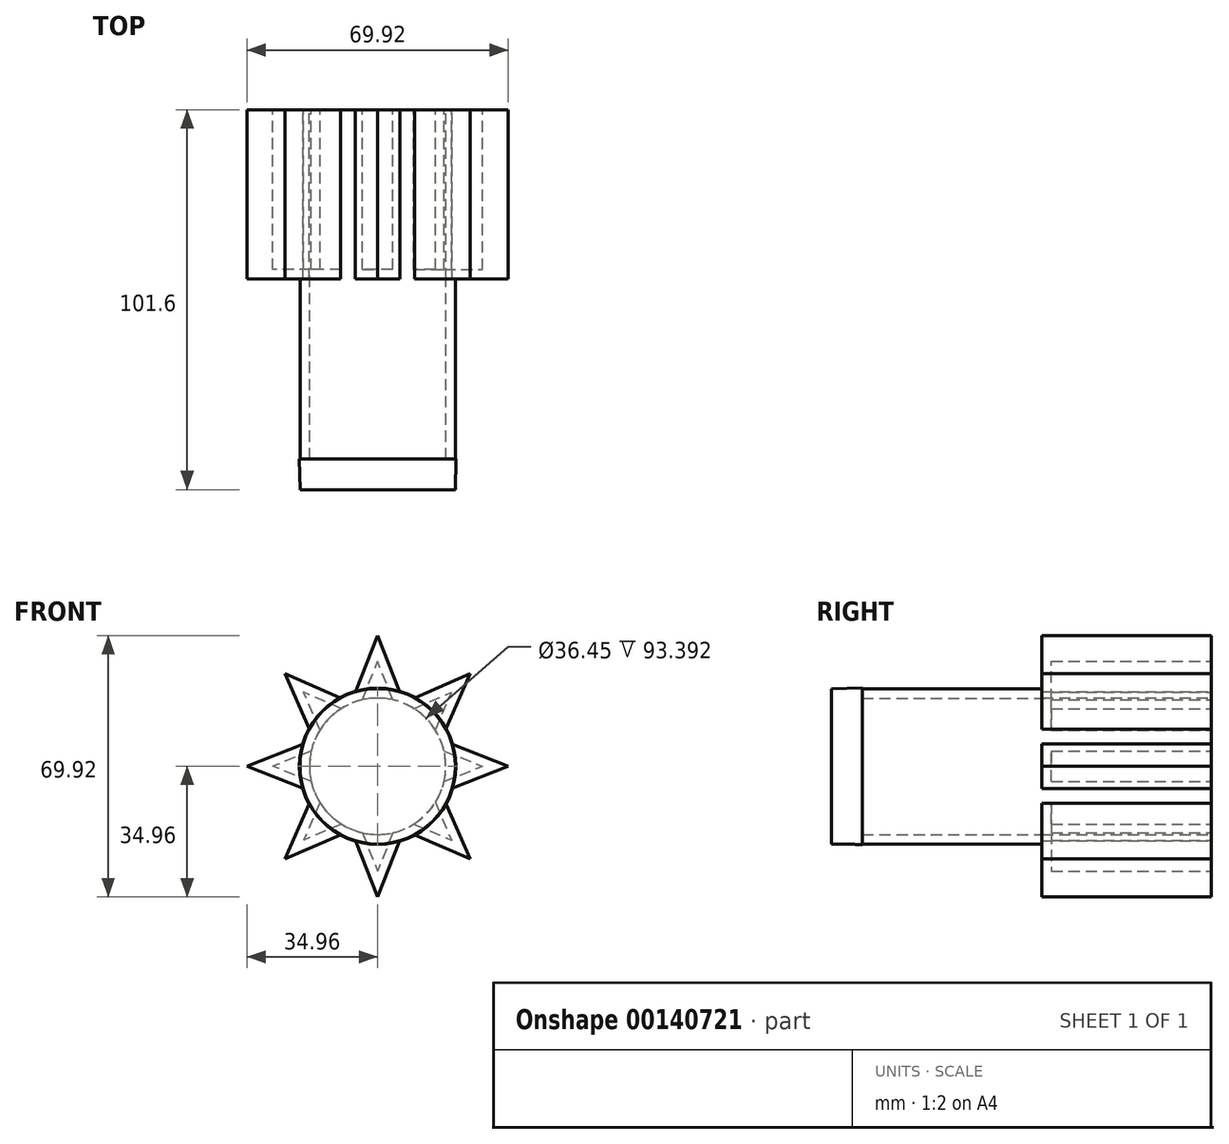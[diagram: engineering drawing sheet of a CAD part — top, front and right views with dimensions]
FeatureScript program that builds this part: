
annotation { "Feature Type Name" : "Feature", "Feature Type Description" : "" }
export const myFeature = defineFeature(function(context is Context, id is Id, definition is map)
    precondition{}
    {
        {
            var Q0;
            Q0=qCreatedBy(makeId("Front.planeOp"),FACE);
            var sketch = newSketch(context, id + "F0", { "sketchPlane" : qUnion([Q0])});
            skCircle(sketch, "E0", {"center": v(0, 0) * mm, "radius": 20.77 * mm});
            skSolve(sketch);
        }
        {
            var Q0;
            Q0 = qSketchRegion(id + "F0", true);
            extrude(context, id + "F1", {"entities" : qUnion([Q0]), "depth" : 101.6 * mm});
        }
        {
            var Q0;
            Q0=makeQuery(id+"F1.opExtrude","CAP_FACE",FACE,{"disambiguationData":[OSD([sQuery(id+"F0.wireOp",EDGE,"E0")])],"isStart":true});
            var sketch = newSketch(context, id + "F2", { "sketchPlane" : qUnion([Q0])});
            skLineSegment(sketch, "E1", {"start": v(-5.94, 19.9) * mm, "end": v(0, 34.96) * mm});
            skLineSegment(sketch, "E2", {"start": v(0, 34.96) * mm, "end": v(-5.94, 19.9) * mm});
            skLineSegment(sketch, "E3", {"start": v(-5.94, 19.9) * mm, "end": v(5.94, 19.9) * mm});
            skLineSegment(sketch, "E4", {"start": v(5.94, 19.9) * mm, "end": v(0, 34.96) * mm});
            skLineSegment(sketch, "E5", {"start": v(0, 19.9) * mm, "end": v(0, 0) * mm, "construction": true});
            skSolve(sketch);
        }
        {
            var Q0;
            Q0 = qSketchRegion(id + "F2", true);
            extrude(context, id + "F3", {"entities" : qUnion([Q0]), "operationType" : NewBodyOperationType.ADD, "oppositeDirection" : true, "depth" : 45.3 * mm});
        }
        {
            var Q0;
            Q0=makeQuery(id+"F1.opExtrude","SWEPT_BODY",BODY,{"disambiguationData":[OSD([sQuery(id+"F0.wireOp",EDGE,"E0")])]});
            var Q1;
            Q1=makeQuery(id+"F1.opExtrude","SWEPT_FACE",FACE,{"disambiguationData":[OSD([sQuery(id+"F0.wireOp",EDGE,"E0")])]});
            circularPattern(context, id + "F4", {"entities" : qUnion([Q0]), "axis" : qUnion([Q1]), "angle" : 45 * degree, "instanceCount" : 8});
        }
        {
            var Q0;
            Q0=makeQuery(id+"F4.opPattern","COPY",BODY,{"derivedFrom":makeQuery(id+"F1.opExtrude","SWEPT_BODY",BODY,{"disambiguationData":[OSD([sQuery(id+"F0.wireOp",EDGE,"E0")])]}),"instanceName":"3"});
            var Q1;
            Q1=makeQuery(id+"F1.opExtrude","SWEPT_BODY",BODY,{"disambiguationData":[OSD([sQuery(id+"F0.wireOp",EDGE,"E0")])]});
            var Q2;
            Q2=makeQuery(id+"F4.opPattern","COPY",BODY,{"derivedFrom":makeQuery(id+"F1.opExtrude","SWEPT_BODY",BODY,{"disambiguationData":[OSD([sQuery(id+"F0.wireOp",EDGE,"E0")])]}),"instanceName":"7"});
            var Q3;
            Q3=makeQuery(id+"F4.opPattern","COPY",BODY,{"derivedFrom":makeQuery(id+"F1.opExtrude","SWEPT_BODY",BODY,{"disambiguationData":[OSD([sQuery(id+"F0.wireOp",EDGE,"E0")])]}),"instanceName":"5"});
            var Q4;
            Q4=makeQuery(id+"F4.opPattern","COPY",BODY,{"derivedFrom":makeQuery(id+"F1.opExtrude","SWEPT_BODY",BODY,{"disambiguationData":[OSD([sQuery(id+"F0.wireOp",EDGE,"E0")])]}),"instanceName":"1"});
            var Q5;
            Q5=makeQuery(id+"F4.opPattern","COPY",BODY,{"derivedFrom":makeQuery(id+"F1.opExtrude","SWEPT_BODY",BODY,{"disambiguationData":[OSD([sQuery(id+"F0.wireOp",EDGE,"E0")])]}),"instanceName":"2"});
            var Q6;
            Q6=makeQuery(id+"F4.opPattern","COPY",BODY,{"derivedFrom":makeQuery(id+"F1.opExtrude","SWEPT_BODY",BODY,{"disambiguationData":[OSD([sQuery(id+"F0.wireOp",EDGE,"E0")])]}),"instanceName":"4"});
            var Q7;
            Q7=makeQuery(id+"F4.opPattern","COPY",BODY,{"derivedFrom":makeQuery(id+"F1.opExtrude","SWEPT_BODY",BODY,{"disambiguationData":[OSD([sQuery(id+"F0.wireOp",EDGE,"E0")])]}),"instanceName":"6"});
            booleanBodies(context, id + "F5", {"operationType" : BooleanOperationType.UNION, "tools" : qUnion([Q0, Q1, Q2, Q3, Q4, Q5, Q6, Q7])});
        }
        {
            var Q0;
            {var subQ0=makeQuery(id+"F3.boolean.opBoolean","MERGE",FACE,{"derivedFrom":[makeQuery(id+"F1.opExtrude","CAP_FACE",FACE,{"disambiguationData":[OSD([sQuery(id+"F0.wireOp",EDGE,"E0")])],"isStart":true}),makeQuery(id+"F3.opExtrude","CAP_FACE",FACE,{"disambiguationData":[OSD([sQuery(id+"F2.wireOp",EDGE,"E2"),sQuery(id+"F2.wireOp",EDGE,"E3"),sQuery(id+"F2.wireOp",EDGE,"E4")])],"isStart":true})]});Q0=makeQuery(id+"F5.opBoolean","MERGE",FACE,{"derivedFrom":[subQ0,makeQuery(id+"F4.opPattern","COPY",FACE,{"derivedFrom":subQ0,"instanceName":"1"}),makeQuery(id+"F4.opPattern","COPY",FACE,{"derivedFrom":subQ0,"instanceName":"2"}),makeQuery(id+"F4.opPattern","COPY",FACE,{"derivedFrom":subQ0,"instanceName":"3"}),makeQuery(id+"F4.opPattern","COPY",FACE,{"derivedFrom":subQ0,"instanceName":"4"}),makeQuery(id+"F4.opPattern","COPY",FACE,{"derivedFrom":subQ0,"instanceName":"5"}),makeQuery(id+"F4.opPattern","COPY",FACE,{"derivedFrom":subQ0,"instanceName":"6"}),makeQuery(id+"F4.opPattern","COPY",FACE,{"derivedFrom":subQ0,"instanceName":"7"})]});}
            shell(context, id + "F6", {"entities" : qUnion([Q0]), "thickness" : 2.54 * mm});
        }
        {
            var Q0;
            Q0=makeQuery(id+"F4.opPattern","COPY",FACE,{"derivedFrom":makeQuery(id+"F1.opExtrude","CAP_FACE",FACE,{"disambiguationData":[OSD([sQuery(id+"F0.wireOp",EDGE,"E0")])],"isStart":false}),"instanceName":"3"});
            extrude(context, id + "F7", {"entities" : qUnion([Q0]), "operationType" : NewBodyOperationType.ADD, "oppositeDirection" : true, "depth" : 8.2 * mm, "hasDraft" : true, "draftAngle" : 1 * degree});
        }
    });
